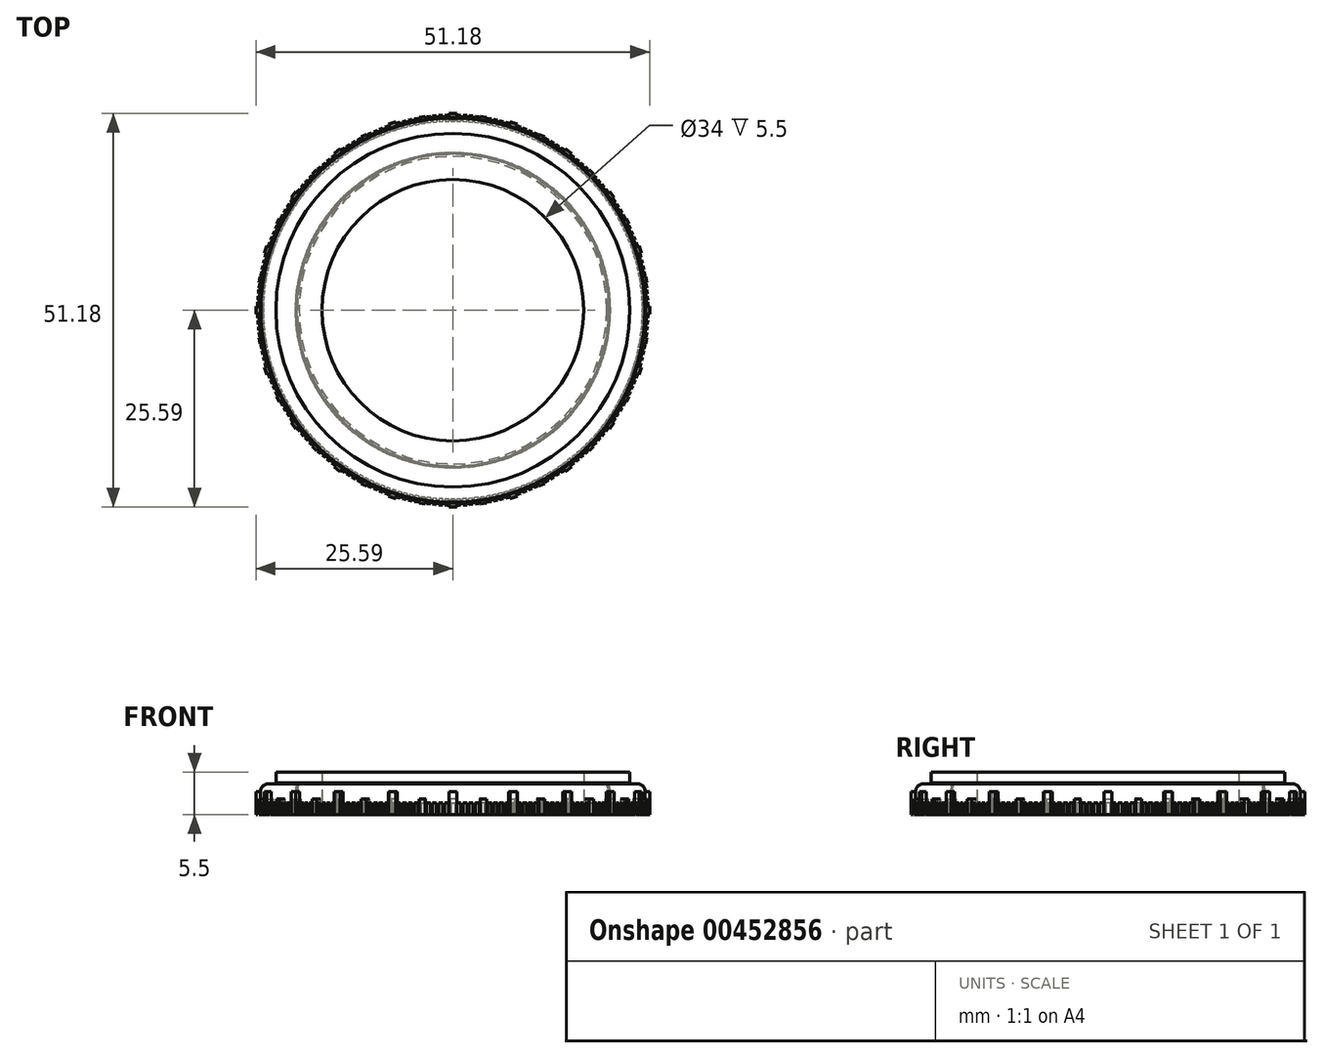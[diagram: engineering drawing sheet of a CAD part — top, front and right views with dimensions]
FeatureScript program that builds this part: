
annotation { "Feature Type Name" : "Feature", "Feature Type Description" : "" }
export const myFeature = defineFeature(function(context is Context, id is Id, definition is map)
    precondition{}
    {
        {
            var Q0;
            Q0=qCreatedBy(makeId("Front.planeOp"),FACE);
            var sketch = newSketch(context, id + "F0", { "sketchPlane" : qUnion([Q0])});
            skLineSegment(sketch, "E0", {"start": v(0, 0) * mm, "end": v(-17, 0) * mm, "construction": true});
            skLineSegment(sketch, "E1", {"start": v(-17, 0) * mm, "end": v(-17, 4) * mm});
            skLineSegment(sketch, "E2", {"start": v(-17, 4) * mm, "end": v(-20, 4) * mm});
            skFitSpline(sketch, "E3", {"points": [v(-20, 4) * mm, v(-20.4, 2) * mm, v(-20, 0) * mm], "startDerivative": vector(-1.2, -4) * mm, "endDerivative": vector(1.2, -4) * mm});
            skLineSegment(sketch, "E4", {"start": v(-20, 0) * mm, "end": v(-17, 0) * mm});
            skLineSegment(sketch, "E5", {"start": v(0, 0) * mm, "end": v(0, 23.06) * mm, "construction": true});
            skLineSegment(sketch, "E6", {"start": v(-20, 4) * mm, "end": v(-20.25, 4) * mm, "construction": true});
            skLineSegment(sketch, "E7", {"start": v(-20.4, 2) * mm, "end": v(-20.9, 2) * mm, "construction": true});
            skFitSpline(sketch, "E8", {"points": [v(-20.25, 4) * mm, v(-20.5, 2) * mm, v(-20.25, 0) * mm], "startDerivative": vector(-0.75, -4) * mm, "endDerivative": vector(0.75, -4) * mm});
            skLineSegment(sketch, "E9", {"start": v(0, 0) * mm, "end": v(-25, 0) * mm, "construction": true});
            skLineSegment(sketch, "E10", {"start": v(-20.25, 0) * mm, "end": v(-25, 0) * mm});
            skLineSegment(sketch, "E11", {"start": v(-25, 0) * mm, "end": v(-25, 4) * mm});
            skLineSegment(sketch, "E12", {"start": v(-25, 4) * mm, "end": v(-20.25, 4) * mm});
            skLineSegment(sketch, "E13", {"start": v(-17, 4) * mm, "end": v(-17, 5.5) * mm});
            skLineSegment(sketch, "E14", {"start": v(-17, 5.5) * mm, "end": v(-23, 5.5) * mm});
            skLineSegment(sketch, "E15", {"start": v(-23, 5.5) * mm, "end": v(-23, 4.1) * mm});
            skLineSegment(sketch, "E16", {"start": v(-23, 4.1) * mm, "end": v(-20, 4.1) * mm});
            skLineSegment(sketch, "E17", {"start": v(-20, 4.1) * mm, "end": v(-20, 4) * mm});
            skSolve(sketch);
        }
        {
            var Q0;
            Q0=makeQuery(id+"F0.imprint","IMPRINT",FACE,{"disambiguationData":[TD([[makeQuery(id+"F0.imprint","IMPRINT",EDGE,{"derivedFrom":sQuery(id+"F0.wireOp",EDGE,"E1")}),1.0]])]});
            var Q1;
            Q1=makeQuery(id+"F0.imprint","IMPRINT",FACE,{"disambiguationData":[TD([[makeQuery(id+"F0.imprint","IMPRINT",EDGE,{"derivedFrom":sQuery(id+"F0.wireOp",EDGE,"E2")}),-1.0]])]});
            var Q2;
            Q2=sQuery(id+"F0.wireOp",EDGE,"E5");
            revolve(context, id + "F1", {"entities" : qUnion([Q0, Q1]), "axis" : qUnion([Q2]), "revolveType" : RevolveType.FULL});
        }
        {
            var Q0;
            Q0=makeQuery(id+"F0.imprint","IMPRINT",FACE,{"disambiguationData":[TD([[makeQuery(id+"F0.imprint","IMPRINT",EDGE,{"derivedFrom":sQuery(id+"F0.wireOp",EDGE,"E8")}),-1.0]])]});
            var Q1;
            Q1=sQuery(id+"F0.wireOp",EDGE,"E5");
            revolve(context, id + "F2", {"entities" : qUnion([Q0]), "axis" : qUnion([Q1]), "revolveType" : RevolveType.FULL});
        }
        {
            var Q0;
            Q0=makeQuery(id+"F2.opRevolve","SWEPT_EDGE",EDGE,{"disambiguationData":[OSD([sQuery(id+"F0.wireOp",EDGE,"E11"),sQuery(id+"F0.wireOp",EDGE,"E12")])]});
            fillet(context, id + "F3", {"entities" : qUnion([Q0]), "radius" : 1 * mm, "tangentPropagation" : true, "allowEdgeOverflow" : false});
        }
        {
            var Q0;
            Q0=qCreatedBy(makeId("Top.planeOp"),FACE);
            var sketch = newSketch(context, id + "F4", { "sketchPlane" : qUnion([Q0])});
            skLineSegment(sketch, "E18.bottom", {"start": v(-24.59, -0.5) * mm, "end": v(-25.59, -0.5) * mm});
            skLineSegment(sketch, "E18.top", {"start": v(-24.59, 0.5) * mm, "end": v(-25.59, 0.5) * mm});
            skLineSegment(sketch, "E18.left", {"start": v(-24.59, -0.5) * mm, "end": v(-24.59, 0.5) * mm});
            skLineSegment(sketch, "E18.right", {"start": v(-25.59, -0.5) * mm, "end": v(-25.59, 0.5) * mm});
            skPoint(sketch, "E18.middle", {"position": v(-25.09, 0) * mm});
            skLineSegment(sketch, "E19.bottom", {"start": v(25.48, -0.4) * mm, "end": v(24.68, -0.4) * mm});
            skLineSegment(sketch, "E19.top", {"start": v(25.48, 0.4) * mm, "end": v(24.68, 0.4) * mm});
            skLineSegment(sketch, "E19.left", {"start": v(25.48, -0.4) * mm, "end": v(25.48, 0.4) * mm});
            skLineSegment(sketch, "E19.right", {"start": v(24.68, -0.4) * mm, "end": v(24.68, 0.4) * mm});
            skPoint(sketch, "E19.middle", {"position": v(25.08, 0) * mm});
            skLineSegment(sketch, "E20.bottom", {"start": v(0.25, -25.38) * mm, "end": v(-0.25, -25.38) * mm});
            skLineSegment(sketch, "E20.top", {"start": v(0.25, -24.58) * mm, "end": v(-0.25, -24.58) * mm});
            skLineSegment(sketch, "E20.left", {"start": v(0.25, -25.38) * mm, "end": v(0.25, -24.58) * mm});
            skLineSegment(sketch, "E20.right", {"start": v(-0.25, -25.38) * mm, "end": v(-0.25, -24.58) * mm});
            skPoint(sketch, "E20.middle", {"position": v(0, -24.98) * mm});
            skSolve(sketch);
        }
        {
            var Q0;
            Q0=makeQuery(id+"F4.imprint","IMPRINT",FACE,{"disambiguationData":[TD([[makeQuery(id+"F4.imprint","IMPRINT",EDGE,{"derivedFrom":sQuery(id+"F4.wireOp",EDGE,"E18.bottom")}),-1.0]])]});
            extrude(context, id + "F5", {"entities" : qUnion([Q0]), "operationType" : NewBodyOperationType.ADD, "depth" : 3 * mm});
        }
        {
            var Q0;
            Q0=makeQuery(id+"F2.opRevolve","SWEPT_BODY",BODY,{"disambiguationData":[OSD([sQuery(id+"F0.wireOp",EDGE,"E8"),sQuery(id+"F0.wireOp",EDGE,"E10"),sQuery(id+"F0.wireOp",EDGE,"E11"),sQuery(id+"F0.wireOp",EDGE,"E12")])]});
            var Q1;
            Q1=sQuery(id+"F0.wireOp",EDGE,"E5");
            circularPattern(context, id + "F6", {"entities" : qUnion([Q0]), "axis" : qUnion([Q1]), "angle" : 360 * degree, "instanceCount" : 20, "equalSpace" : true});
        }
        {
            var Q0;
            Q0=makeQuery(id+"F4.imprint","IMPRINT",FACE,{"disambiguationData":[TD([[makeQuery(id+"F4.imprint","IMPRINT",EDGE,{"derivedFrom":sQuery(id+"F4.wireOp",EDGE,"E19.bottom")}),-1.0]])]});
            extrude(context, id + "F7", {"entities" : qUnion([Q0]), "depth" : 2 * mm});
        }
        {
            var Q0;
            Q0=makeQuery(id+"F7.opExtrude","SWEPT_BODY",BODY,{"disambiguationData":[OSD([sQuery(id+"F4.wireOp",EDGE,"E19.bottom"),sQuery(id+"F4.wireOp",EDGE,"E19.top"),sQuery(id+"F4.wireOp",EDGE,"E19.left"),sQuery(id+"F4.wireOp",EDGE,"E19.right")])]});
            var Q1;
            Q1=sQuery(id+"F0.wireOp",EDGE,"E5");
            circularPattern(context, id + "F8", {"entities" : qUnion([Q0]), "axis" : qUnion([Q1]), "angle" : 360 * degree, "instanceCount" : 40, "equalSpace" : true});
        }
        {
            var Q0;
            Q0=makeQuery(id+"F4.imprint","IMPRINT",FACE,{"disambiguationData":[TD([[makeQuery(id+"F4.imprint","IMPRINT",EDGE,{"derivedFrom":sQuery(id+"F4.wireOp",EDGE,"E20.bottom")}),-1.0]])]});
            extrude(context, id + "F9", {"entities" : qUnion([Q0]), "depth" : 1.5 * mm});
        }
        {
            var Q0;
            Q0=makeQuery(id+"F9.opExtrude","SWEPT_BODY",BODY,{"disambiguationData":[OSD([sQuery(id+"F4.wireOp",EDGE,"E20.bottom"),sQuery(id+"F4.wireOp",EDGE,"E20.top"),sQuery(id+"F4.wireOp",EDGE,"E20.left"),sQuery(id+"F4.wireOp",EDGE,"E20.right")])]});
            var Q1;
            Q1=sQuery(id+"F0.wireOp",EDGE,"E5");
            circularPattern(context, id + "F10", {"entities" : qUnion([Q0]), "axis" : qUnion([Q1]), "angle" : 360 * degree, "instanceCount" : 200, "equalSpace" : true});
        }
    });
